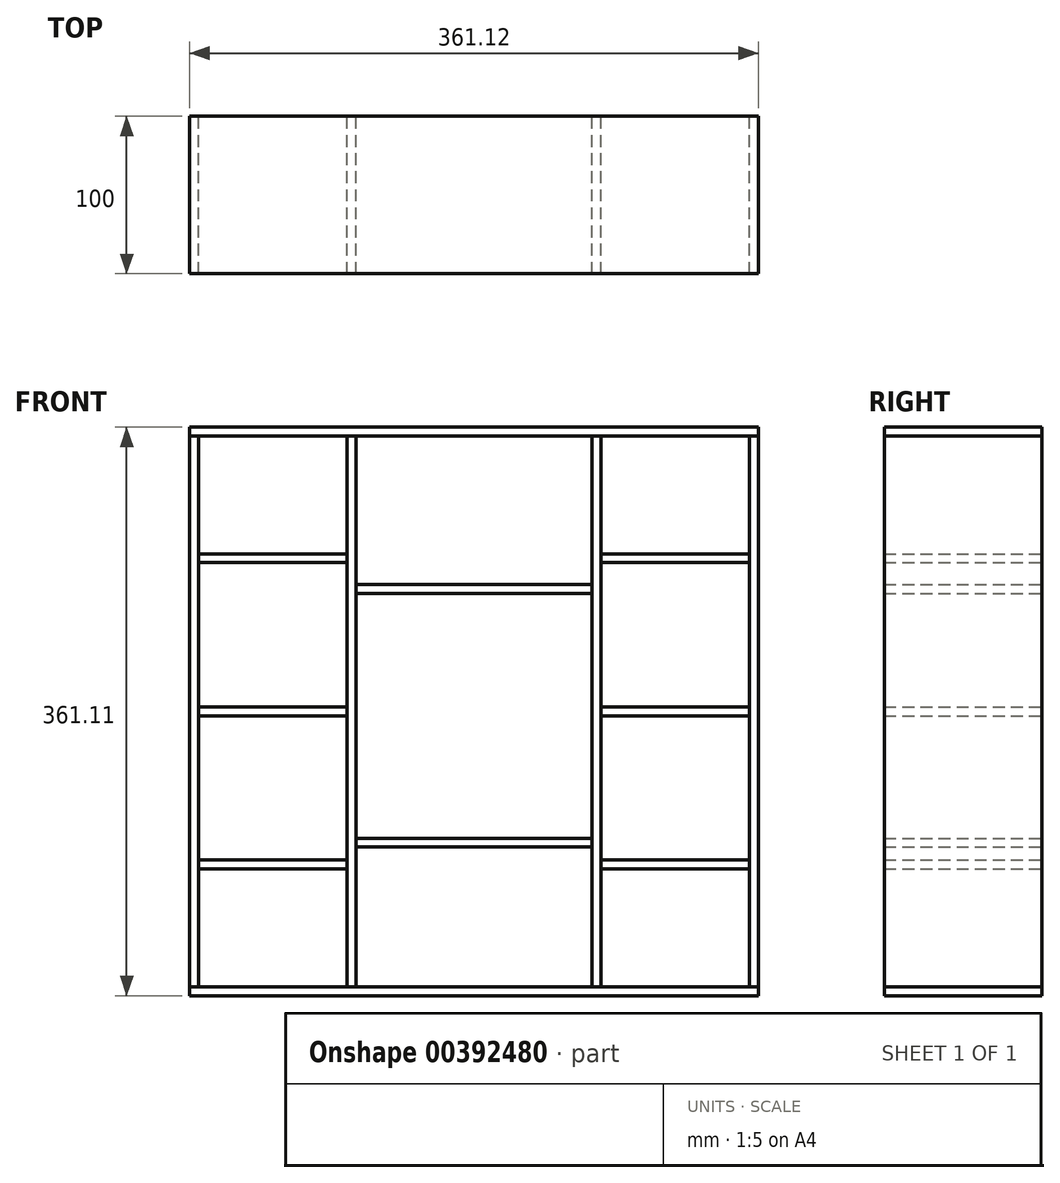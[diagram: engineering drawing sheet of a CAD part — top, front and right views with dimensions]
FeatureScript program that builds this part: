
annotation { "Feature Type Name" : "Feature", "Feature Type Description" : "" }
export const myFeature = defineFeature(function(context is Context, id is Id, definition is map)
    precondition{}
    {
        {
            var Q0;
            Q0=qCreatedBy(makeId("Front.planeOp"),FACE);
            var sketch = newSketch(context, id + "F0", { "sketchPlane" : qUnion([Q0])});
            skLineSegment(sketch, "E0.top", {"start": v(-175, 21.47) * mm, "end": v(175, 21.47) * mm});
            skLineSegment(sketch, "E1.0", {"start": v(-175, -328.53) * mm, "end": v(180.56, -328.53) * mm});
            skLineSegment(sketch, "E2", {"start": v(-175, 21.47) * mm, "end": v(-175, -328.53) * mm});
            skLineSegment(sketch, "E3.0", {"start": v(-180.56, 21.47) * mm, "end": v(-180.56, -328.53) * mm});
            skLineSegment(sketch, "E4.0", {"start": v(175, 21.47) * mm, "end": v(175, -328.53) * mm});
            skLineSegment(sketch, "E5.0", {"start": v(180.56, 21.47) * mm, "end": v(180.56, -328.53) * mm});
            skLineSegment(sketch, "E6", {"start": v(-180.56, 21.47) * mm, "end": v(-175, 21.47) * mm});
            skLineSegment(sketch, "E7", {"start": v(-180.56, 21.47) * mm, "end": v(-180.56, 27.02) * mm});
            skLineSegment(sketch, "E8", {"start": v(175, 21.47) * mm, "end": v(180.56, 21.47) * mm});
            skLineSegment(sketch, "E9", {"start": v(180.56, 21.47) * mm, "end": v(180.56, 27.02) * mm});
            skLineSegment(sketch, "E10", {"start": v(-180.56, -328.53) * mm, "end": v(-175, -328.53) * mm});
            skLineSegment(sketch, "E11", {"start": v(-180.56, -328.53) * mm, "end": v(-180.56, -334.09) * mm});
            skLineSegment(sketch, "E12", {"start": v(-175, -153.53) * mm, "end": v(175, -153.53) * mm, "construction": true});
            skLineSegment(sketch, "E13", {"start": v(0, 21.47) * mm, "end": v(0, -328.53) * mm, "construction": true});
            skLineSegment(sketch, "E14.0", {"start": v(-75, 21.47) * mm, "end": v(-75, -328.53) * mm});
            skLineSegment(sketch, "E15.MirrorCS", {"start": v(75, 21.47) * mm, "end": v(75, -328.53) * mm});
            skLineSegment(sketch, "E16.0", {"start": v(-80.56, 21.47) * mm, "end": v(-80.56, -328.53) * mm});
            skLineSegment(sketch, "E17.0", {"start": v(80.56, 21.47) * mm, "end": v(80.56, -328.53) * mm});
            skLineSegment(sketch, "E18", {"start": v(-75, 21.47) * mm, "end": v(75, 21.47) * mm});
            skLineSegment(sketch, "E19.0", {"start": v(-75, -78.53) * mm, "end": v(75, -78.53) * mm});
            skLineSegment(sketch, "E20.0", {"start": v(-75, -72.98) * mm, "end": v(75, -72.98) * mm});
            skLineSegment(sketch, "E21.MirrorCS", {"start": v(-75, -234.09) * mm, "end": v(75, -234.09) * mm});
            skLineSegment(sketch, "E22", {"start": v(80.56, 21.47) * mm, "end": v(175, 21.47) * mm});
            skLineSegment(sketch, "E23.0", {"start": v(80.56, -53.53) * mm, "end": v(175, -53.53) * mm});
            skLineSegment(sketch, "E24.0", {"start": v(80.56, -59.09) * mm, "end": v(175, -59.09) * mm});
            skLineSegment(sketch, "E25", {"start": v(175, -153.53) * mm, "end": v(80.56, -153.53) * mm, "construction": true});
            skLineSegment(sketch, "E26.0", {"start": v(175, -156.3) * mm, "end": v(80.56, -156.3) * mm});
            skLineSegment(sketch, "E27.0", {"start": v(175, -150.75) * mm, "end": v(80.56, -150.75) * mm});
            skLineSegment(sketch, "E28.MirrorCS", {"start": v(80.56, -253.53) * mm, "end": v(175, -253.53) * mm});
            skLineSegment(sketch, "E29.MirrorCS", {"start": v(80.56, -247.98) * mm, "end": v(175, -247.98) * mm});
            skLineSegment(sketch, "E30.MirrorCS", {"start": v(-80.56, -53.53) * mm, "end": v(-175, -53.53) * mm});
            skLineSegment(sketch, "E31.MirrorCS", {"start": v(-80.56, -59.09) * mm, "end": v(-175, -59.09) * mm});
            skLineSegment(sketch, "E32.MirrorCS", {"start": v(-175, -150.75) * mm, "end": v(-80.56, -150.75) * mm});
            skLineSegment(sketch, "E33.MirrorCS", {"start": v(-175, -156.3) * mm, "end": v(-80.56, -156.3) * mm});
            skLineSegment(sketch, "E34.MirrorCS", {"start": v(-80.56, -247.98) * mm, "end": v(-175, -247.98) * mm});
            skLineSegment(sketch, "E35.MirrorCS", {"start": v(-80.56, -253.53) * mm, "end": v(-175, -253.53) * mm});
            skLineSegment(sketch, "E36.0", {"start": v(-75, -239.64) * mm, "end": v(75, -239.64) * mm});
            skLineSegment(sketch, "E37", {"start": v(180.56, -328.53) * mm, "end": v(180.56, -334.09) * mm});
            skLineSegment(sketch, "E38", {"start": v(-180.56, -334.09) * mm, "end": v(180.56, -334.09) * mm});
            skLineSegment(sketch, "E39", {"start": v(-180.56, 27.02) * mm, "end": v(180.56, 27.02) * mm});
            skSolve(sketch);
        }
        {
            var Q0;
            {var subQ4=sQuery(id+"F0.wireOp",EDGE,"E6");Q0=makeQuery(id+"F0.imprint","IMPRINT",FACE,{"disambiguationData":[TD([[makeQuery(id+"F0.imprint","IMPRINT",EDGE,{"derivedFrom":subQ4}),1.0]])]});}
            extrude(context, id + "F1", {"entities" : qUnion([Q0]), "depth" : 100 * mm});
        }
        {
            var Q0;
            {var subQ5=sQuery(id+"F0.wireOp",EDGE,"E10");Q0=makeQuery(id+"F0.imprint","IMPRINT",FACE,{"disambiguationData":[TD([[makeQuery(id+"F0.imprint","IMPRINT",EDGE,{"derivedFrom":subQ5}),-1.0]])]});}
            extrude(context, id + "F2", {"entities" : qUnion([Q0]), "depth" : 100 * mm});
        }
        {
            var Q0;
            {var subQ3=sQuery(id+"F0.wireOp",EDGE,"E5.0");Q0=makeQuery(id+"F0.imprint","IMPRINT",FACE,{"disambiguationData":[TD([[makeQuery(id+"F0.imprint","IMPRINT",EDGE,{"derivedFrom":subQ3}),-1.0]])]});}
            extrude(context, id + "F3", {"entities" : qUnion([Q0]), "depth" : 100 * mm});
        }
        {
            var Q0;
            Q0=makeQuery(id+"F0.imprint","IMPRINT",FACE,{"disambiguationData":[TD([[makeQuery(id+"F0.imprint","IMPRINT",EDGE,{"derivedFrom":sQuery(id+"F0.wireOp",EDGE,"E3.0")}),1.0]])]});
            extrude(context, id + "F4", {"entities" : qUnion([Q0]), "depth" : 100 * mm});
        }
        {
            var Q0;
            {var subQ4=sQuery(id+"F0.wireOp",EDGE,"E14.0");var subQ5=sQuery(id+"F0.wireOp",EDGE,"E1.0");var subQ6=makeQuery(id+"F0.imprint","INTERSECT",VERTEX,{"derivedFrom":[subQ5,subQ4]});Q0=makeQuery(id+"F0.imprint","IMPRINT",FACE,{"disambiguationData":[TD([[makeQuery(id+"F0.imprint","IMPRINT",EDGE,{"disambiguationData":[TD([[subQ6,1.0]])],"derivedFrom":subQ5}),1.0]])]});}
            extrude(context, id + "F5", {"entities" : qUnion([Q0]), "depth" : 100 * mm});
        }
        {
            var Q0;
            {var subQ0=sQuery(id+"F0.wireOp",EDGE,"E15.MirrorCS");var subQ1=sQuery(id+"F0.wireOp",EDGE,"E1.0");var subQ2=makeQuery(id+"F0.imprint","INTERSECT",VERTEX,{"derivedFrom":[subQ1,subQ0]});Q0=makeQuery(id+"F0.imprint","IMPRINT",FACE,{"disambiguationData":[TD([[makeQuery(id+"F0.imprint","IMPRINT",EDGE,{"disambiguationData":[TD([[subQ2,-1.0]])],"derivedFrom":subQ1}),1.0]])]});}
            extrude(context, id + "F6", {"entities" : qUnion([Q0]), "depth" : 100 * mm});
        }
        {
            var Q0;
            {var subQ0=sQuery(id+"F0.wireOp",EDGE,"E30.MirrorCS");Q0=makeQuery(id+"F0.imprint","IMPRINT",FACE,{"disambiguationData":[TD([[makeQuery(id+"F0.imprint","IMPRINT",EDGE,{"derivedFrom":subQ0}),1.0]])]});}
            var Q1;
            {var subQ0=sQuery(id+"F0.wireOp",EDGE,"E32.MirrorCS");Q1=makeQuery(id+"F0.imprint","IMPRINT",FACE,{"disambiguationData":[TD([[makeQuery(id+"F0.imprint","IMPRINT",EDGE,{"derivedFrom":subQ0}),-1.0]])]});}
            var Q2;
            {var subQ0=sQuery(id+"F0.wireOp",EDGE,"E34.MirrorCS");Q2=makeQuery(id+"F0.imprint","IMPRINT",FACE,{"disambiguationData":[TD([[makeQuery(id+"F0.imprint","IMPRINT",EDGE,{"derivedFrom":subQ0}),1.0]])]});}
            var Q3;
            {var subQ0=sQuery(id+"F0.wireOp",EDGE,"E19.0");Q3=makeQuery(id+"F0.imprint","IMPRINT",FACE,{"disambiguationData":[TD([[makeQuery(id+"F0.imprint","IMPRINT",EDGE,{"derivedFrom":subQ0}),1.0]])]});}
            var Q4;
            {var subQ0=sQuery(id+"F0.wireOp",EDGE,"E21.MirrorCS");Q4=makeQuery(id+"F0.imprint","IMPRINT",FACE,{"disambiguationData":[TD([[makeQuery(id+"F0.imprint","IMPRINT",EDGE,{"derivedFrom":subQ0}),-1.0]])]});}
            var Q5;
            {var subQ0=sQuery(id+"F0.wireOp",EDGE,"E23.0");Q5=makeQuery(id+"F0.imprint","IMPRINT",FACE,{"disambiguationData":[TD([[makeQuery(id+"F0.imprint","IMPRINT",EDGE,{"derivedFrom":subQ0}),-1.0]])]});}
            var Q6;
            {var subQ0=sQuery(id+"F0.wireOp",EDGE,"E26.0");Q6=makeQuery(id+"F0.imprint","IMPRINT",FACE,{"disambiguationData":[TD([[makeQuery(id+"F0.imprint","IMPRINT",EDGE,{"derivedFrom":subQ0}),-1.0]])]});}
            var Q7;
            {var subQ0=sQuery(id+"F0.wireOp",EDGE,"E28.MirrorCS");Q7=makeQuery(id+"F0.imprint","IMPRINT",FACE,{"disambiguationData":[TD([[makeQuery(id+"F0.imprint","IMPRINT",EDGE,{"derivedFrom":subQ0}),1.0]])]});}
            extrude(context, id + "F7", {"entities" : qUnion([Q0, Q1, Q2, Q3, Q4, Q5, Q6, Q7]), "depth" : 100 * mm});
        }
    });
